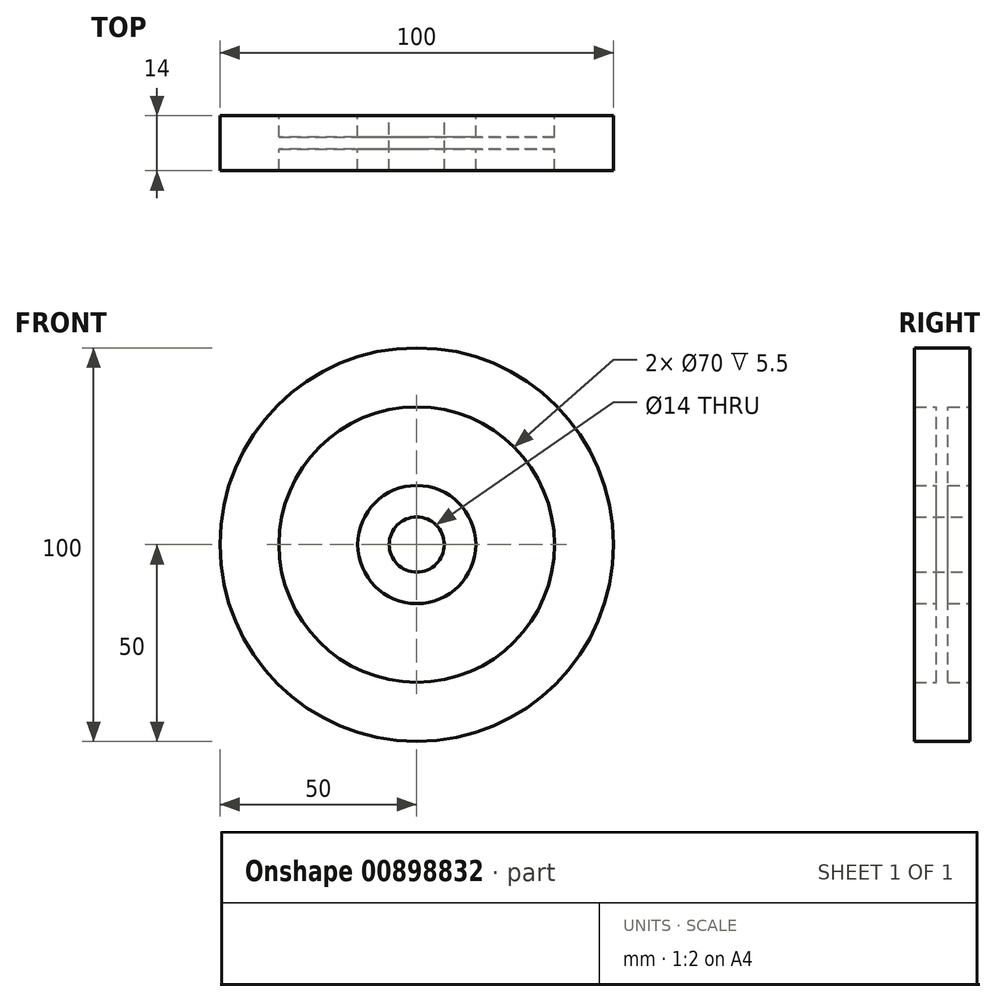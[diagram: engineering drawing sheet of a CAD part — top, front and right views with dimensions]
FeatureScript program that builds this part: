
annotation { "Feature Type Name" : "Feature", "Feature Type Description" : "" }
export const myFeature = defineFeature(function(context is Context, id is Id, definition is map)
    precondition{}
    {
        {
            var Q0;
            Q0=qCreatedBy(makeId("Front.planeOp"),FACE);
            var sketch = newSketch(context, id + "F0", { "sketchPlane" : qUnion([Q0])});
            skCircle(sketch, "E0", {"center": v(0, 0) * mm, "radius": 15 * mm});
            skCircle(sketch, "E1", {"center": v(0, 0) * mm, "radius": 7 * mm});
            skCircle(sketch, "E2", {"center": v(0, 0) * mm, "radius": 35 * mm});
            skCircle(sketch, "E3", {"center": v(0, 0) * mm, "radius": 50 * mm});
            skSolve(sketch);
        }
        {
            var Q0;
            Q0=makeQuery(id+"F0.imprint","IMPRINT",FACE,{"disambiguationData":[TD([[makeQuery(id+"F0.imprint","IMPRINT",EDGE,{"derivedFrom":sQuery(id+"F0.wireOp",EDGE,"E0")}),-1.0]])]});
            extrude(context, id + "F1", {"entities" : qUnion([Q0]), "endBound" : BoundingType.SYMMETRIC, "depth" : 3 * mm, "offsetDistance" : 25 * mm, "hasDraft" : true, "draftAngle" : 3 * degree});
        }
        {
            var Q0;
            Q0=makeQuery(id+"F0.imprint","IMPRINT",FACE,{"disambiguationData":[TD([[makeQuery(id+"F0.imprint","IMPRINT",EDGE,{"derivedFrom":sQuery(id+"F0.wireOp",EDGE,"E2")}),-1.0]])]});
            extrude(context, id + "F2", {"entities" : qUnion([Q0]), "operationType" : NewBodyOperationType.ADD, "endBound" : BoundingType.SYMMETRIC, "depth" : 14 * mm, "offsetDistance" : 25 * mm});
        }
        {
            var Q0;
            Q0=makeQuery(id+"F0.imprint","IMPRINT",FACE,{"disambiguationData":[TD([[makeQuery(id+"F0.imprint","IMPRINT",EDGE,{"derivedFrom":sQuery(id+"F0.wireOp",EDGE,"E0")}),1.0]])]});
            extrude(context, id + "F3", {"entities" : qUnion([Q0]), "operationType" : NewBodyOperationType.ADD, "endBound" : BoundingType.SYMMETRIC, "depth" : 14 * mm, "offsetDistance" : 25 * mm});
        }
    });
